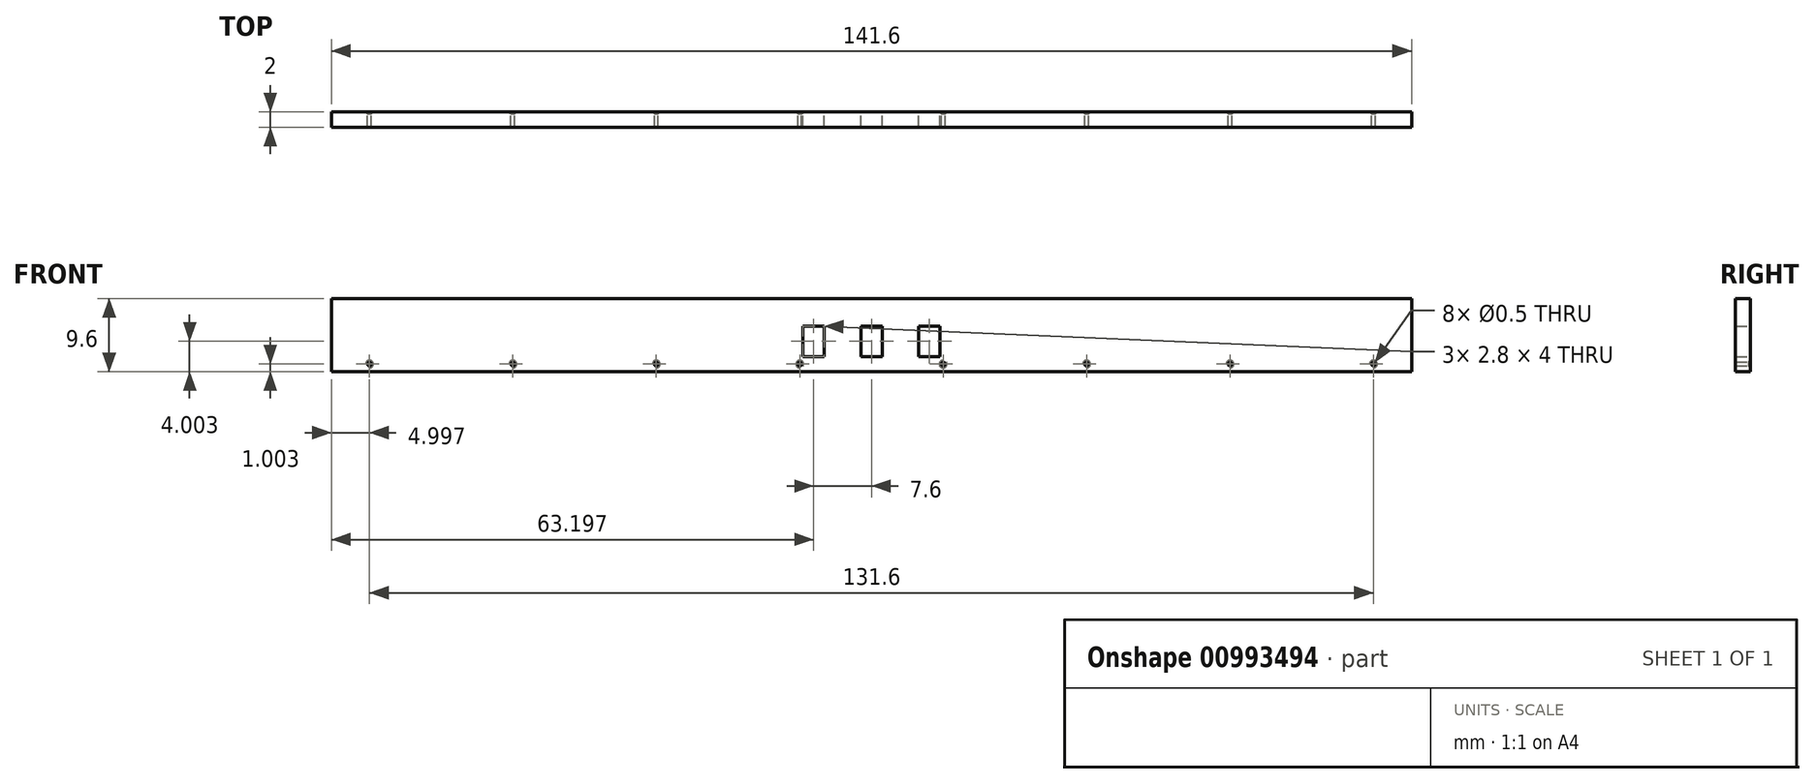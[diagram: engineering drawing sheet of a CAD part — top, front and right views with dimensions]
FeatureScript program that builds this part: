
annotation { "Feature Type Name" : "Feature", "Feature Type Description" : "" }
export const myFeature = defineFeature(function(context is Context, id is Id, definition is map)
    precondition{}
    {
        {
            var Q0;
            Q0=qCreatedBy(makeId("Front.planeOp"),FACE);
            var sketch = newSketch(context, id + "F0", { "sketchPlane" : qUnion([Q0])});
            skLineSegment(sketch, "E0", {"start": v(-73.07, 15.82) * mm, "end": v(68.53, 15.82) * mm});
            skLineSegment(sketch, "E1", {"start": v(68.53, 15.82) * mm, "end": v(68.53, 6.22) * mm});
            skLineSegment(sketch, "E2", {"start": v(-73.07, 6.22) * mm, "end": v(-73.07, 15.82) * mm});
            skLineSegment(sketch, "E3", {"start": v(68.53, 6.22) * mm, "end": v(6.73, 6.22) * mm});
            skLineSegment(sketch, "E4", {"start": v(6.73, 6.22) * mm, "end": v(6.73, 12.22) * mm});
            skLineSegment(sketch, "E5", {"start": v(6.73, 12.22) * mm, "end": v(3.93, 12.22) * mm});
            skLineSegment(sketch, "E6", {"start": v(3.93, 12.22) * mm, "end": v(3.93, 6.22) * mm});
            skLineSegment(sketch, "E7", {"start": v(3.93, 6.22) * mm, "end": v(-0.87, 6.22) * mm});
            skLineSegment(sketch, "E8", {"start": v(-0.87, 6.22) * mm, "end": v(-0.87, 12.22) * mm});
            skLineSegment(sketch, "E9", {"start": v(-0.87, 12.22) * mm, "end": v(-3.67, 12.22) * mm});
            skLineSegment(sketch, "E10", {"start": v(-3.67, 12.22) * mm, "end": v(-3.67, 6.22) * mm});
            skLineSegment(sketch, "E11", {"start": v(-3.67, 6.22) * mm, "end": v(-8.47, 6.22) * mm});
            skLineSegment(sketch, "E12", {"start": v(-8.47, 6.22) * mm, "end": v(-8.47, 12.22) * mm});
            skLineSegment(sketch, "E13", {"start": v(-8.47, 12.22) * mm, "end": v(-11.27, 12.22) * mm});
            skLineSegment(sketch, "E14", {"start": v(-11.27, 12.22) * mm, "end": v(-11.27, 6.22) * mm});
            skLineSegment(sketch, "E15.trimOffspring", {"start": v(-11.27, 6.22) * mm, "end": v(-73.07, 6.22) * mm});
            skPoint(sketch, "E16", {"position": v(-68.07, 7.22) * mm});
            skPoint(sketch, "E17", {"position": v(-49.27, 7.22) * mm});
            skPoint(sketch, "E18", {"position": v(-30.47, 7.22) * mm});
            skPoint(sketch, "E19", {"position": v(-11.67, 7.22) * mm});
            skPoint(sketch, "E20", {"position": v(7.13, 7.22) * mm});
            skPoint(sketch, "E21", {"position": v(25.93, 7.22) * mm});
            skPoint(sketch, "E22", {"position": v(44.73, 7.22) * mm});
            skPoint(sketch, "E23", {"position": v(63.53, 7.22) * mm});
            skLineSegment(sketch, "E24", {"start": v(-11.27, 6.22) * mm, "end": v(-8.47, 6.22) * mm});
            skLineSegment(sketch, "E25", {"start": v(-11.27, 6.22) * mm, "end": v(-11.27, 8.22) * mm});
            skLineSegment(sketch, "E26", {"start": v(-11.27, 8.22) * mm, "end": v(-8.47, 8.22) * mm});
            skLineSegment(sketch, "E27", {"start": v(-3.67, 8.22) * mm, "end": v(-0.87, 8.22) * mm});
            skLineSegment(sketch, "E28", {"start": v(3.93, 8.22) * mm, "end": v(6.73, 8.22) * mm});
            skLineSegment(sketch, "E29", {"start": v(-3.67, 6.22) * mm, "end": v(-0.87, 6.22) * mm});
            skLineSegment(sketch, "E30", {"start": v(3.93, 6.22) * mm, "end": v(6.73, 6.22) * mm});
            skSolve(sketch);
        }
        {
            var Q0;
            Q0=makeQuery(id+"F0.imprint","IMPRINT",FACE,{"disambiguationData":[TD([[makeQuery(id+"F0.imprint","IMPRINT",EDGE,{"derivedFrom":sQuery(id+"F0.wireOp",EDGE,"E0")}),-1.0]])]});
            extrude(context, id + "F1", {"entities" : qUnion([Q0]), "depth" : 2 * mm, "offsetDistance" : 25 * mm});
        }
        {
            var Q0;
            Q0=sQuery(id+"F0.wireOp",VERTEX,"E23");
            var Q1;
            Q1=sQuery(id+"F0.wireOp",VERTEX,"E22");
            var Q2;
            Q2=sQuery(id+"F0.wireOp",VERTEX,"E21");
            var Q3;
            Q3=sQuery(id+"F0.wireOp",VERTEX,"E20");
            var Q4;
            Q4=sQuery(id+"F0.wireOp",VERTEX,"E19");
            var Q5;
            Q5=sQuery(id+"F0.wireOp",VERTEX,"E18");
            var Q6;
            Q6=sQuery(id+"F0.wireOp",VERTEX,"E17");
            var Q7;
            Q7=sQuery(id+"F0.wireOp",VERTEX,"E16");
            var Q8;
            Q8=makeQuery(id+"F1.opExtrude","SWEPT_BODY",BODY,{"disambiguationData":[OSD([sQuery(id+"F0.wireOp",EDGE,"E0"),sQuery(id+"F0.wireOp",EDGE,"E1"),sQuery(id+"F0.wireOp",EDGE,"E2"),sQuery(id+"F0.wireOp",EDGE,"E3"),sQuery(id+"F0.wireOp",EDGE,"E4"),sQuery(id+"F0.wireOp",EDGE,"E5"),sQuery(id+"F0.wireOp",EDGE,"E6"),sQuery(id+"F0.wireOp",EDGE,"E8"),sQuery(id+"F0.wireOp",EDGE,"E9"),sQuery(id+"F0.wireOp",EDGE,"E10"),sQuery(id+"F0.wireOp",EDGE,"E12"),sQuery(id+"F0.wireOp",EDGE,"E13"),sQuery(id+"F0.wireOp",EDGE,"E14"),sQuery(id+"F0.wireOp",EDGE,"E15.trimOffspring"),sQuery(id+"F0.wireOp",EDGE,"E11"),sQuery(id+"F0.wireOp",EDGE,"E7")])]});
            hole(context, id + "F2", {"style" : HoleStyle.C_SINK, "endStyle" : HoleEndStyle.THROUGH, "oppositeDirection" : true, "holeDiameter" : 0.5 * mm, "cSinkDiameter" : 1 * mm, "cSinkAngle" : 90 * degree, "majorDiameter" : 5 * mm, "isTappedThrough" : true, "tappedDepth" : 12 * mm, "tapClearance" : 3, "locations" : qUnion([Q0, Q1, Q2, Q3, Q4, Q5, Q6, Q7]), "scope" : qUnion([Q8])});
        }
        {
            var Q0;
            {var subQ0=sQuery(id+"F0.wireOp",EDGE,"E24");Q0=makeQuery(id+"F0.imprint","IMPRINT",FACE,{"disambiguationData":[TD([[makeQuery(id+"F0.imprint","IMPRINT",EDGE,{"derivedFrom":subQ0}),1.0]])]});}
            var Q1;
            {var subQ2=sQuery(id+"F0.wireOp",EDGE,"E27");Q1=makeQuery(id+"F0.imprint","IMPRINT",FACE,{"disambiguationData":[TD([[makeQuery(id+"F0.imprint","IMPRINT",EDGE,{"derivedFrom":subQ2}),-1.0]])]});}
            var Q2;
            {var subQ2=sQuery(id+"F0.wireOp",EDGE,"E28");Q2=makeQuery(id+"F0.imprint","IMPRINT",FACE,{"disambiguationData":[TD([[makeQuery(id+"F0.imprint","IMPRINT",EDGE,{"derivedFrom":subQ2}),-1.0]])]});}
            extrude(context, id + "F3", {"entities" : qUnion([Q0, Q1, Q2]), "operationType" : NewBodyOperationType.ADD, "depth" : 2 * mm, "offsetDistance" : 25 * mm});
        }
    });
